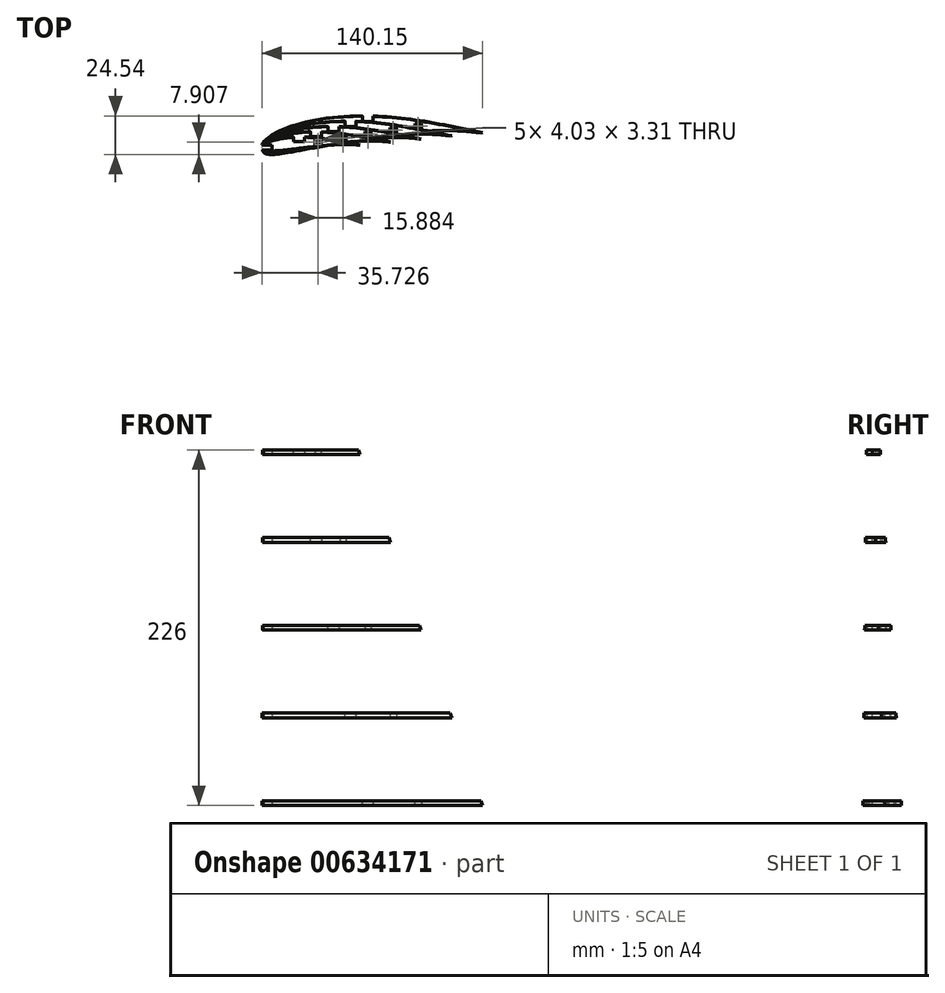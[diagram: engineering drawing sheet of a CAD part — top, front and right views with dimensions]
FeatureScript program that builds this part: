
annotation { "Feature Type Name" : "Feature", "Feature Type Description" : "" }
export const myFeature = defineFeature(function(context is Context, id is Id, definition is map)
    precondition{}
    {
        {
            var Q0;
            Q0=qCreatedBy(makeId("Top.planeOp"),FACE);
            var sketch = newSketch(context, id + "F0", { "sketchPlane" : qUnion([Q0])});
            skLineSegment(sketch, "E0", {"start": v(-0.42, 1.1) * mm, "end": v(1.04, 2.87) * mm});
            skLineSegment(sketch, "E1", {"start": v(1.04, 2.87) * mm, "end": v(2.54, 4.58) * mm});
            skLineSegment(sketch, "E2", {"start": v(2.54, 4.58) * mm, "end": v(4.15, 6.16) * mm});
            skLineSegment(sketch, "E3", {"start": v(4.15, 6.16) * mm, "end": v(4.64, 6.58) * mm});
            skLineSegment(sketch, "E4", {"start": v(4.64, 6.58) * mm, "end": v(5.9, 7.56) * mm});
            skLineSegment(sketch, "E5", {"start": v(5.9, 7.56) * mm, "end": v(7.8, 8.78) * mm});
            skLineSegment(sketch, "E6", {"start": v(7.8, 8.78) * mm, "end": v(9.8, 9.86) * mm});
            skLineSegment(sketch, "E7", {"start": v(9.8, 9.86) * mm, "end": v(11.89, 10.8) * mm});
            skLineSegment(sketch, "E8", {"start": v(11.89, 10.8) * mm, "end": v(15.88, 12.34) * mm});
            skLineSegment(sketch, "E9", {"start": v(15.88, 12.34) * mm, "end": v(18.36, 13.2) * mm});
            skLineSegment(sketch, "E10", {"start": v(18.36, 13.2) * mm, "end": v(22.7, 14.6) * mm});
            skLineSegment(sketch, "E11", {"start": v(22.7, 14.6) * mm, "end": v(27.05, 15.83) * mm});
            skLineSegment(sketch, "E12", {"start": v(27.05, 15.83) * mm, "end": v(32.46, 17.12) * mm});
            skLineSegment(sketch, "E13", {"start": v(32.46, 17.12) * mm, "end": v(35.87, 17.8) * mm});
            skLineSegment(sketch, "E14", {"start": v(35.87, 17.8) * mm, "end": v(40.34, 18.53) * mm});
            skLineSegment(sketch, "E15", {"start": v(40.34, 18.53) * mm, "end": v(44.84, 19.11) * mm});
            skLineSegment(sketch, "E16", {"start": v(44.84, 19.11) * mm, "end": v(49.37, 19.56) * mm});
            skLineSegment(sketch, "E17", {"start": v(49.37, 19.56) * mm, "end": v(52.55, 19.79) * mm});
            skLineSegment(sketch, "E18", {"start": v(52.55, 19.79) * mm, "end": v(58.48, 20.07) * mm});
            skLineSegment(sketch, "E19", {"start": v(58.48, 20.07) * mm, "end": v(63.03, 20.16) * mm});
            skLineSegment(sketch, "E20", {"start": v(63.03, 20.16) * mm, "end": v(67.58, 20.14) * mm});
            skLineSegment(sketch, "E21", {"start": v(67.58, 20.14) * mm, "end": v(72.1, 20.03) * mm});
            skLineSegment(sketch, "E22", {"start": v(72.1, 20.03) * mm, "end": v(74.6, 19.93) * mm});
            skLineSegment(sketch, "E23", {"start": v(74.6, 19.93) * mm, "end": v(81.02, 19.54) * mm});
            skLineSegment(sketch, "E24", {"start": v(81.02, 19.54) * mm, "end": v(85.48, 19.16) * mm});
            skLineSegment(sketch, "E25", {"start": v(85.48, 19.16) * mm, "end": v(90, 18.69) * mm});
            skLineSegment(sketch, "E26", {"start": v(90, 18.69) * mm, "end": v(96.67, 17.82) * mm});
            skLineSegment(sketch, "E27", {"start": v(96.67, 17.82) * mm, "end": v(99.3, 17.44) * mm});
            skLineSegment(sketch, "E28", {"start": v(99.3, 17.44) * mm, "end": v(104.05, 16.68) * mm});
            skLineSegment(sketch, "E29", {"start": v(104.05, 16.68) * mm, "end": v(108.68, 15.9) * mm});
            skLineSegment(sketch, "E30", {"start": v(108.68, 15.9) * mm, "end": v(110.9, 15.5) * mm});
            skLineSegment(sketch, "E31", {"start": v(110.9, 15.5) * mm, "end": v(113.04, 15.11) * mm});
            skLineSegment(sketch, "E32", {"start": v(113.04, 15.11) * mm, "end": v(115.07, 14.74) * mm});
            skLineSegment(sketch, "E33", {"start": v(115.07, 14.74) * mm, "end": v(116.62, 14.45) * mm});
            skLineSegment(sketch, "E34", {"start": v(116.62, 14.45) * mm, "end": v(120.51, 13.7) * mm});
            skLineSegment(sketch, "E35", {"start": v(120.51, 13.7) * mm, "end": v(122.38, 13.34) * mm});
            skLineSegment(sketch, "E36", {"start": v(122.38, 13.34) * mm, "end": v(123.38, 13.14) * mm});
            skLineSegment(sketch, "E37", {"start": v(123.38, 13.14) * mm, "end": v(124.45, 12.92) * mm});
            skLineSegment(sketch, "E38", {"start": v(124.45, 12.92) * mm, "end": v(125.6, 12.68) * mm});
            skLineSegment(sketch, "E39", {"start": v(125.6, 12.68) * mm, "end": v(126.84, 12.43) * mm});
            skLineSegment(sketch, "E40", {"start": v(126.84, 12.43) * mm, "end": v(128.18, 12.15) * mm});
            skLineSegment(sketch, "E41", {"start": v(128.18, 12.15) * mm, "end": v(129.65, 11.84) * mm});
            skLineSegment(sketch, "E42", {"start": v(129.65, 11.84) * mm, "end": v(131.93, 11.36) * mm});
            skLineSegment(sketch, "E43", {"start": v(131.93, 11.36) * mm, "end": v(133, 11.13) * mm});
            skLineSegment(sketch, "E44", {"start": v(133, 11.13) * mm, "end": v(134.82, 10.75) * mm});
            skLineSegment(sketch, "E45", {"start": v(134.82, 10.75) * mm, "end": v(136.58, 10.37) * mm});
            skLineSegment(sketch, "E46", {"start": v(136.58, 10.37) * mm, "end": v(137.4, 10.2) * mm});
            skLineSegment(sketch, "E47", {"start": v(137.4, 10.2) * mm, "end": v(138.16, 10.03) * mm});
            skLineSegment(sketch, "E48", {"start": v(138.16, 10.03) * mm, "end": v(138.83, 9.88) * mm});
            skLineSegment(sketch, "E49", {"start": v(138.83, 9.88) * mm, "end": v(139.4, 9.75) * mm});
            skLineSegment(sketch, "E50", {"start": v(139.4, 9.75) * mm, "end": v(139.86, 9.65) * mm});
            skLineSegment(sketch, "E51", {"start": v(139.86, 9.65) * mm, "end": v(140.2, 9.56) * mm});
            skLineSegment(sketch, "E52", {"start": v(140.2, 9.56) * mm, "end": v(140.38, 9.51) * mm});
            skLineSegment(sketch, "E53", {"start": v(140.38, 9.51) * mm, "end": v(140.4, 9.5) * mm});
            skLineSegment(sketch, "E54", {"start": v(140.4, 9.5) * mm, "end": v(140.24, 9.5) * mm});
            skLineSegment(sketch, "E55", {"start": v(140.24, 9.5) * mm, "end": v(140.08, 9.53) * mm});
            skLineSegment(sketch, "E56", {"start": v(140.08, 9.53) * mm, "end": v(139.36, 9.65) * mm});
            skLineSegment(sketch, "E57", {"start": v(139.36, 9.65) * mm, "end": v(138.4, 9.81) * mm});
            skLineSegment(sketch, "E58", {"start": v(138.4, 9.81) * mm, "end": v(136.21, 10.13) * mm});
            skLineSegment(sketch, "E59", {"start": v(136.21, 10.13) * mm, "end": v(133.85, 10.4) * mm});
            skLineSegment(sketch, "E60", {"start": v(133.85, 10.4) * mm, "end": v(131.61, 10.58) * mm});
            skLineSegment(sketch, "E61", {"start": v(131.61, 10.58) * mm, "end": v(126.03, 10.8) * mm});
            skLineSegment(sketch, "E62", {"start": v(126.03, 10.8) * mm, "end": v(122.98, 10.85) * mm});
            skLineSegment(sketch, "E63", {"start": v(122.98, 10.85) * mm, "end": v(118.52, 10.88) * mm});
            skLineSegment(sketch, "E64", {"start": v(118.52, 10.88) * mm, "end": v(113.95, 10.85) * mm});
            skLineSegment(sketch, "E65", {"start": v(113.95, 10.85) * mm, "end": v(109.34, 10.75) * mm});
            skLineSegment(sketch, "E66", {"start": v(109.34, 10.75) * mm, "end": v(103.97, 10.52) * mm});
            skLineSegment(sketch, "E67", {"start": v(103.97, 10.52) * mm, "end": v(100.13, 10.27) * mm});
            skLineSegment(sketch, "E68", {"start": v(100.13, 10.27) * mm, "end": v(95.58, 9.9) * mm});
            skLineSegment(sketch, "E69", {"start": v(95.58, 9.9) * mm, "end": v(91.07, 9.44) * mm});
            skLineSegment(sketch, "E70", {"start": v(91.07, 9.44) * mm, "end": v(86.57, 8.91) * mm});
            skLineSegment(sketch, "E71", {"start": v(86.57, 8.91) * mm, "end": v(76.85, 7.57) * mm});
            skLineSegment(sketch, "E72", {"start": v(76.85, 7.57) * mm, "end": v(68.73, 6.27) * mm});
            skLineSegment(sketch, "E73", {"start": v(68.73, 6.27) * mm, "end": v(59.8, 4.7) * mm});
            skLineSegment(sketch, "E74", {"start": v(59.8, 4.7) * mm, "end": v(49.88, 2.79) * mm});
            skLineSegment(sketch, "E75", {"start": v(49.88, 2.79) * mm, "end": v(41.82, 1.14) * mm});
            skLineSegment(sketch, "E76", {"start": v(41.82, 1.14) * mm, "end": v(37.34, 0.22) * mm});
            skLineSegment(sketch, "E77", {"start": v(37.34, 0.22) * mm, "end": v(32.9, -0.65) * mm});
            skLineSegment(sketch, "E78", {"start": v(32.9, -0.65) * mm, "end": v(26.98, -1.7) * mm});
            skLineSegment(sketch, "E79", {"start": v(26.98, -1.7) * mm, "end": v(24.24, -2.14) * mm});
            skLineSegment(sketch, "E80", {"start": v(24.24, -2.14) * mm, "end": v(19.94, -2.77) * mm});
            skLineSegment(sketch, "E81", {"start": v(19.94, -2.77) * mm, "end": v(17.73, -3.06) * mm});
            skLineSegment(sketch, "E82", {"start": v(17.73, -3.06) * mm, "end": v(15.45, -3.36) * mm});
            skLineSegment(sketch, "E83", {"start": v(15.45, -3.36) * mm, "end": v(13.08, -3.65) * mm});
            skLineSegment(sketch, "E84", {"start": v(13.08, -3.65) * mm, "end": v(10.68, -3.96) * mm});
            skLineSegment(sketch, "E85", {"start": v(10.68, -3.96) * mm, "end": v(8.03, -4.25) * mm});
            skLineSegment(sketch, "E86", {"start": v(8.03, -4.25) * mm, "end": v(6.75, -4.33) * mm});
            skLineSegment(sketch, "E87", {"start": v(6.75, -4.33) * mm, "end": v(5.52, -4.33) * mm});
            skLineSegment(sketch, "E88", {"start": v(5.52, -4.33) * mm, "end": v(4.36, -4.21) * mm});
            skLineSegment(sketch, "E89", {"start": v(4.36, -4.21) * mm, "end": v(3.3, -3.97) * mm});
            skLineSegment(sketch, "E90", {"start": v(3.3, -3.97) * mm, "end": v(2.34, -3.56) * mm});
            skLineSegment(sketch, "E91", {"start": v(2.34, -3.56) * mm, "end": v(1.92, -3.28) * mm});
            skLineSegment(sketch, "E92", {"start": v(1.92, -3.28) * mm, "end": v(1.4, -2.83) * mm});
            skLineSegment(sketch, "E93", {"start": v(1.4, -2.83) * mm, "end": v(1.19, -2.58) * mm});
            skLineSegment(sketch, "E94", {"start": v(1.19, -2.58) * mm, "end": v(0.89, -2.15) * mm});
            skLineSegment(sketch, "E95", {"start": v(0.89, -2.15) * mm, "end": v(0.38, -1.16) * mm});
            skLineSegment(sketch, "E96", {"start": v(0.38, -1.16) * mm, "end": v(-0.05, -0.06) * mm});
            skLineSegment(sketch, "E97", {"start": v(-0.05, -0.06) * mm, "end": v(-0.42, 1.1) * mm});
            skSolve(sketch);
        }
        {
            var Q0;
            Q0=qCreatedBy(makeId("Top.planeOp"),FACE);
            var sketch = newSketch(context, id + "F1", { "sketchPlane" : qUnion([Q0])});
            skPoint(sketch, "E98.0", {"position": v(0.94, -2.52) * mm});
            skPoint(sketch, "E98.1", {"position": v(0.64, -2.08) * mm});
            skPoint(sketch, "E98.2", {"position": v(0.13, -1.1) * mm});
            skPoint(sketch, "E98.3", {"position": v(0.8, 2.93) * mm});
            skPoint(sketch, "E98.5", {"position": v(40.1, 18.6) * mm});
            skPoint(sketch, "E98.6", {"position": v(85.24, 19.22) * mm});
            skPoint(sketch, "E98.7", {"position": v(140.15, 9.56) * mm});
            skPoint(sketch, "E98.8", {"position": v(125.78, 10.86) * mm});
            skPoint(sketch, "E98.9", {"position": v(99.89, 10.34) * mm});
            skPoint(sketch, "E98.10", {"position": v(49.63, 2.85) * mm});
            skPoint(sketch, "E98.11", {"position": v(12.84, -3.6) * mm});
            skPoint(sketch, "E98.12", {"position": v(2.1, -3.5) * mm});
            skPoint(sketch, "E98.13", {"position": v(5.28, -4.26) * mm});
            skFitSpline(sketch, "E99", {"points": [v(0.94, -2.52) * mm, v(2.1, -3.5) * mm, v(5.28, -4.26) * mm, v(12.84, -3.6) * mm, v(49.63, 2.85) * mm, v(99.89, 10.34) * mm, v(125.78, 10.86) * mm, v(140.15, 9.56) * mm], "startDerivative": vector(21.8, -23.84) * mm, "endDerivative": vector(100.11, -11.16) * mm});
            skPoint(sketch, "E100.0", {"position": v(11.64, 10.87) * mm});
            skFitSpline(sketch, "E101", {"points": [v(0.94, -2.52) * mm, v(0.64, -2.08) * mm, v(0.13, -1.1) * mm, v(0.8, 2.93) * mm, v(11.64, 10.87) * mm, v(40.1, 18.6) * mm, v(85.24, 19.22) * mm, v(140.15, 9.56) * mm], "startDerivative": vector(-10.5, 15.16) * mm, "endDerivative": vector(201.75, -43.18) * mm});
            skSolve(sketch);
        }
        {
            var Q0;
            Q0=qCreatedBy(makeId("Top.planeOp"),FACE);
            cPlane(context, id + "F2", {"entities" : qUnion([Q0]), "cplaneType" : CPlaneType.OFFSET, "offset" : 226 * mm, "width" : 150 * mm, "height" : 150 * mm});
        }
        {
            var Q0;
            Q0=qCreatedBy(id+"F2.planeOp",FACE);
            var sketch = newSketch(context, id + "F3", { "sketchPlane" : qUnion([Q0])});
            skPoint(sketch, "E102.0", {"position": v(0.64, -1.21) * mm});
            skPoint(sketch, "E102.1", {"position": v(0.07, -0.47) * mm});
            skPoint(sketch, "E102.2", {"position": v(0.27, 1.18) * mm});
            skPoint(sketch, "E102.3", {"position": v(2.53, 3.05) * mm});
            skPoint(sketch, "E102.4", {"position": v(15.91, 6.32) * mm});
            skPoint(sketch, "E102.5", {"position": v(32.82, 6.27) * mm});
            skPoint(sketch, "E102.6", {"position": v(61.27, 1.72) * mm});
            skPoint(sketch, "E102.7", {"position": v(55.5, 2.19) * mm});
            skPoint(sketch, "E102.8", {"position": v(33.37, 0.87) * mm});
            skPoint(sketch, "E102.9", {"position": v(18.25, -1.04) * mm});
            skPoint(sketch, "E102.10", {"position": v(10.5, -1.8) * mm});
            skPoint(sketch, "E102.11", {"position": v(1.43, -1.7) * mm});
            skPoint(sketch, "E102.12", {"position": v(2.88, -2) * mm});
            skFitSpline(sketch, "E103", {"points": [v(0.64, -1.21) * mm, v(0.07, -0.47) * mm, v(0.27, 1.18) * mm, v(2.53, 3.05) * mm, v(15.91, 6.32) * mm, v(32.82, 6.27) * mm, v(61.27, 1.72) * mm], "startDerivative": vector(-12.39, 11.02) * mm, "endDerivative": vector(97.43, -17.58) * mm});
            skFitSpline(sketch, "E104", {"points": [v(0.64, -1.21) * mm, v(1.43, -1.7) * mm, v(2.88, -2) * mm, v(10.5, -1.8) * mm, v(18.25, -1.04) * mm, v(33.37, 0.87) * mm, v(55.5, 2.19) * mm, v(61.27, 1.72) * mm], "startDerivative": vector(14.9, -10.52) * mm, "endDerivative": vector(36.47, -4.99) * mm});
            skSolve(sketch);
        }
        {
            var Q0;
            Q0=makeQuery(id+"F1.imprint","IMPRINT",FACE,{"disambiguationData":[TD([[makeQuery(id+"F1.imprint","IMPRINT",EDGE,{"derivedFrom":sQuery(id+"F1.wireOp",EDGE,"E99")}),1.0]])]});
            var Q1;
            Q1=makeQuery(id+"F3.imprint","IMPRINT",FACE,{"disambiguationData":[TD([[makeQuery(id+"F3.imprint","IMPRINT",EDGE,{"derivedFrom":sQuery(id+"F3.wireOp",EDGE,"E103")}),-1.0]])]});
            loft(context, id + "F4", {"sheetProfilesArray" : [{ "sheetProfileEntities" : qUnion([Q0]) }, { "sheetProfileEntities" : qUnion([Q1]) }]});
        }
        {
            var Q0;
            Q0=qCreatedBy(makeId("Front.planeOp"),FACE);
            var sketch = newSketch(context, id + "F5", { "sketchPlane" : qUnion([Q0])});
            skLineSegment(sketch, "E105", {"start": v(0, 0) * mm, "end": v(0, 3) * mm, "construction": true});
            skLineSegment(sketch, "E106.bottom", {"start": v(-6.3, 3) * mm, "end": v(175.34, 3) * mm});
            skLineSegment(sketch, "E106.top", {"start": v(-6.3, 55.75) * mm, "end": v(175.34, 55.75) * mm});
            skLineSegment(sketch, "E106.left", {"start": v(-6.3, 3) * mm, "end": v(-6.3, 55.75) * mm});
            skLineSegment(sketch, "E106.right", {"start": v(175.34, 3) * mm, "end": v(175.34, 55.75) * mm});
            skLineSegment(sketch, "E107.0.1.0", {"start": v(175.34, 58.75) * mm, "end": v(175.34, 111.5) * mm});
            skLineSegment(sketch, "E107.0.1.1", {"start": v(-6.3, 58.75) * mm, "end": v(-6.3, 111.5) * mm});
            skLineSegment(sketch, "E107.0.1.2", {"start": v(-6.3, 58.75) * mm, "end": v(175.34, 58.75) * mm});
            skLineSegment(sketch, "E107.0.1.3", {"start": v(-6.3, 111.5) * mm, "end": v(175.34, 111.5) * mm});
            skLineSegment(sketch, "E107.0.1.4", {"start": v(0, 55.75) * mm, "end": v(0, 58.75) * mm, "construction": true});
            skLineSegment(sketch, "E107.0.2.0", {"start": v(175.34, 114.5) * mm, "end": v(175.34, 167.25) * mm});
            skLineSegment(sketch, "E107.0.2.1", {"start": v(-6.3, 114.5) * mm, "end": v(-6.3, 167.25) * mm});
            skLineSegment(sketch, "E107.0.2.2", {"start": v(-6.3, 114.5) * mm, "end": v(175.34, 114.5) * mm});
            skLineSegment(sketch, "E107.0.2.3", {"start": v(-6.3, 167.25) * mm, "end": v(175.34, 167.25) * mm});
            skLineSegment(sketch, "E107.0.2.4", {"start": v(0, 111.5) * mm, "end": v(0, 114.5) * mm, "construction": true});
            skLineSegment(sketch, "E107.0.3.0", {"start": v(175.34, 170.25) * mm, "end": v(175.34, 223) * mm});
            skLineSegment(sketch, "E107.0.3.1", {"start": v(-6.3, 170.25) * mm, "end": v(-6.3, 223) * mm});
            skLineSegment(sketch, "E107.0.3.2", {"start": v(-6.3, 170.25) * mm, "end": v(175.34, 170.25) * mm});
            skLineSegment(sketch, "E107.0.3.3", {"start": v(-6.3, 223) * mm, "end": v(175.34, 223) * mm});
            skLineSegment(sketch, "E107.0.3.4", {"start": v(0, 167.25) * mm, "end": v(0, 170.25) * mm, "construction": true});
            skLineSegment(sketch, "E107.direction1", {"start": v(-6.3, 3) * mm, "end": v(18.7, 3) * mm, "construction": true});
            skLineSegment(sketch, "E107.direction2", {"start": v(-6.3, 3) * mm, "end": v(-6.3, 58.75) * mm, "construction": true});
            skSolve(sketch);
        }
        {
            var Q0;
            Q0 = qSketchRegion(id + "F5", true);
            extrude(context, id + "F6", {"entities" : qUnion([Q0]), "operationType" : NewBodyOperationType.REMOVE, "oppositeDirection" : true, "depth" : 50 * mm, "offsetDistance" : 25 * mm, "hasSecondDirection" : true, "secondDirectionOppositeDirection" : false, "secondDirectionDepth" : 50 * mm});
        }
        {
            var Q0;
            Q0=qCreatedBy(makeId("Top.planeOp"),FACE);
            var sketch = newSketch(context, id + "F7", { "sketchPlane" : qUnion([Q0])});
            skLineSegment(sketch, "E108", {"start": v(0, 0) * mm, "end": v(6.35, 0) * mm, "construction": true});
            skLineSegment(sketch, "E109", {"start": v(6.35, 0) * mm, "end": v(6.35, 1.59) * mm});
            skLineSegment(sketch, "E110", {"start": v(6.35, 0) * mm, "end": v(6.35, -1.59) * mm});
            skLineSegment(sketch, "E111", {"start": v(6.35, -1.59) * mm, "end": v(0, -1.59) * mm});
            skLineSegment(sketch, "E112", {"start": v(0, -1.59) * mm, "end": v(0, 1.59) * mm});
            skLineSegment(sketch, "E113", {"start": v(0, 1.59) * mm, "end": v(6.35, 1.59) * mm});
            skSolve(sketch);
        }
        {
            var Q0;
            Q0 = qSketchRegion(id + "F7", true);
            extrude(context, id + "F8", {"entities" : qUnion([Q0]), "operationType" : NewBodyOperationType.REMOVE, "depth" : 226 * mm, "offsetDistance" : 25 * mm});
        }
        {
            var Q0;
            Q0=makeQuery(id+"F4.opLoft","CAP_FACE",FACE,{"disambiguationData":[OSD([makeQuery(id+"F1.imprint","IMPRINT",FACE,{"disambiguationData":[TD([[makeQuery(id+"F1.imprint","IMPRINT",EDGE,{"derivedFrom":sQuery(id+"F1.wireOp",EDGE,"E99")}),1.0]])]})])],"isStart":true});
            var sketch = newSketch(context, id + "F9", { "sketchPlane" : qUnion([Q0])});
            skPoint(sketch, "E114.0", {"position": v(67.58, -20.14) * mm});
            skLineSegment(sketch, "E115", {"start": v(67.58, -20.14) * mm, "end": v(67.58, -16.97) * mm, "construction": true});
            skLineSegment(sketch, "E116", {"start": v(67.58, -16.97) * mm, "end": v(64.4, -16.97) * mm});
            skLineSegment(sketch, "E117", {"start": v(67.58, -16.97) * mm, "end": v(70.75, -16.97) * mm});
            skLineSegment(sketch, "E118", {"start": v(70.75, -16.97) * mm, "end": v(70.75, -20.47) * mm});
            skLineSegment(sketch, "E119", {"start": v(70.75, -20.47) * mm, "end": v(64.4, -20.47) * mm});
            skLineSegment(sketch, "E120", {"start": v(64.4, -20.47) * mm, "end": v(64.4, -16.97) * mm});
            skSolve(sketch);
        }
        {
            var Q0;
            Q0=makeQuery(id+"F3.imprint","IMPRINT",FACE,{"disambiguationData":[TD([[makeQuery(id+"F3.imprint","IMPRINT",EDGE,{"derivedFrom":sQuery(id+"F3.wireOp",EDGE,"E103")}),-1.0]])]});
            var sketch = newSketch(context, id + "F10", { "sketchPlane" : qUnion([Q0])});
            skFitSpline(sketch, "E121.0", {"points": [v(62.32, 1.83) * mm, v(59.72, 2.3) * mm, v(54.52, 3.24) * mm, v(46.72, 4.6) * mm, v(40.2, 5.61) * mm, v(34.96, 6.3) * mm, v(31.03, 6.7) * mm, v(27.08, 6.97) * mm, v(23.1, 7.03) * mm, v(19.18, 6.84) * mm, v(15.94, 6.47) * mm, v(13.37, 6.05) * mm, v(11.45, 5.7) * mm, v(9.54, 5.29) * mm, v(7.63, 4.82) * mm, v(5.74, 4.3) * mm, v(4.17, 3.78) * mm, v(2.93, 3.29) * mm, v(2.18, 2.93) * mm, v(1.6, 2.6) * mm, v(1.19, 2.31) * mm, v(0.81, 1.98) * mm, v(0.6, 1.73) * mm, v(0.5, 1.59) * mm]});
            skLineSegment(sketch, "E122", {"start": v(23.23, 7) * mm, "end": v(23.23, 3.82) * mm, "construction": true});
            skLineSegment(sketch, "E123", {"start": v(23.23, 3.82) * mm, "end": v(26.4, 3.82) * mm});
            skLineSegment(sketch, "E124", {"start": v(23.23, 3.82) * mm, "end": v(20.06, 3.82) * mm});
            skLineSegment(sketch, "E125", {"start": v(26.4, 3.82) * mm, "end": v(26.4, 7.32) * mm});
            skLineSegment(sketch, "E126", {"start": v(26.4, 7.32) * mm, "end": v(20.06, 7.32) * mm});
            skLineSegment(sketch, "E127", {"start": v(20.06, 7.32) * mm, "end": v(20.06, 3.82) * mm});
            skSolve(sketch);
        }
        {
            var Q0;
            Q0=makeQuery(id+"F1.imprint","IMPRINT",FACE,{"disambiguationData":[TD([[makeQuery(id+"F1.imprint","IMPRINT",EDGE,{"derivedFrom":sQuery(id+"F1.wireOp",EDGE,"E99")}),1.0]])]});
            var sketch = newSketch(context, id + "F11", { "sketchPlane" : qUnion([Q0])});
            skPoint(sketch, "E128.0", {"position": v(70.75, 16.97) * mm});
            skPoint(sketch, "E128.1", {"position": v(64.4, 16.97) * mm});
            skPoint(sketch, "E128.2", {"position": v(64.4, 20.47) * mm});
            skPoint(sketch, "E128.3", {"position": v(70.75, 20.47) * mm});
            skLineSegment(sketch, "E129", {"start": v(70.75, 20.47) * mm, "end": v(70.75, 16.97) * mm});
            skLineSegment(sketch, "E130", {"start": v(70.75, 16.97) * mm, "end": v(64.4, 16.97) * mm});
            skLineSegment(sketch, "E131", {"start": v(64.4, 16.97) * mm, "end": v(64.4, 20.47) * mm});
            skLineSegment(sketch, "E132", {"start": v(64.4, 20.47) * mm, "end": v(70.75, 20.47) * mm});
            skSolve(sketch);
        }
        {
            var Q0;
            Q0=makeQuery(id+"F3.imprint","IMPRINT",FACE,{"disambiguationData":[TD([[makeQuery(id+"F3.imprint","IMPRINT",EDGE,{"derivedFrom":sQuery(id+"F3.wireOp",EDGE,"E103")}),-1.0]])]});
            var sketch = newSketch(context, id + "F12", { "sketchPlane" : qUnion([Q0])});
            skPoint(sketch, "E133.0", {"position": v(20.06, 7.32) * mm});
            skPoint(sketch, "E133.1", {"position": v(20.06, 3.82) * mm});
            skPoint(sketch, "E133.2", {"position": v(26.4, 3.82) * mm});
            skPoint(sketch, "E133.3", {"position": v(26.4, 7.32) * mm});
            skLineSegment(sketch, "E134.bottom", {"start": v(20.06, 3.82) * mm, "end": v(26.4, 3.82) * mm});
            skLineSegment(sketch, "E134.top", {"start": v(20.06, 7.32) * mm, "end": v(26.4, 7.32) * mm});
            skLineSegment(sketch, "E134.left", {"start": v(20.06, 3.82) * mm, "end": v(20.06, 7.32) * mm});
            skLineSegment(sketch, "E134.right", {"start": v(26.4, 3.82) * mm, "end": v(26.4, 7.32) * mm});
            skSolve(sketch);
        }
        {
            var Q0;
            Q0 = qSketchRegion(id + "F11", true);
            var Q1;
            Q1 = qSketchRegion(id + "F12", true);
            loft(context, id + "F13", {"operationType" : NewBodyOperationType.REMOVE, "sheetProfilesArray" : [{ "sheetProfileEntities" : qUnion([Q0]) }, { "sheetProfileEntities" : qUnion([Q1]) }]});
        }
        {
            var Q0;
            Q0=makeQuery(id+"F1.imprint","IMPRINT",FACE,{"disambiguationData":[TD([[makeQuery(id+"F1.imprint","IMPRINT",EDGE,{"derivedFrom":sQuery(id+"F1.wireOp",EDGE,"E99")}),1.0]])]});
            var sketch = newSketch(context, id + "F14", { "sketchPlane" : qUnion([Q0])});
            skLineSegment(sketch, "E135.bottom", {"start": v(101.28, 15.47) * mm, "end": v(98.1, 15.47) * mm});
            skLineSegment(sketch, "E135.top", {"start": v(101.28, 12.3) * mm, "end": v(98.1, 12.3) * mm});
            skLineSegment(sketch, "E135.left", {"start": v(101.28, 15.47) * mm, "end": v(101.28, 12.3) * mm});
            skLineSegment(sketch, "E135.right", {"start": v(98.1, 15.47) * mm, "end": v(98.1, 12.3) * mm});
            skSolve(sketch);
        }
        {
            var Q0;
            Q0=makeQuery(id+"F3.imprint","IMPRINT",FACE,{"disambiguationData":[TD([[makeQuery(id+"F3.imprint","IMPRINT",EDGE,{"derivedFrom":sQuery(id+"F3.wireOp",EDGE,"E103")}),-1.0]])]});
            var sketch = newSketch(context, id + "F15", { "sketchPlane" : qUnion([Q0])});
            skLineSegment(sketch, "E136.bottom", {"start": v(33.71, 5.13) * mm, "end": v(36.89, 5.13) * mm});
            skLineSegment(sketch, "E136.top", {"start": v(33.71, 1.95) * mm, "end": v(36.89, 1.95) * mm});
            skLineSegment(sketch, "E136.left", {"start": v(33.71, 5.13) * mm, "end": v(33.71, 1.95) * mm});
            skLineSegment(sketch, "E136.right", {"start": v(36.89, 5.13) * mm, "end": v(36.89, 1.95) * mm});
            skSolve(sketch);
        }
        {
            var Q0;
            Q0 = qSketchRegion(id + "F14", true);
            var Q1;
            Q1 = qSketchRegion(id + "F15", true);
            loft(context, id + "F16", {"operationType" : NewBodyOperationType.REMOVE, "sheetProfilesArray" : [{ "sheetProfileEntities" : qUnion([Q0]) }, { "sheetProfileEntities" : qUnion([Q1]) }]});
        }
        {
            var Q0;
            Q0=makeQuery(id+"F4.opLoft","CAP_FACE",FACE,{"disambiguationData":[OSD([makeQuery(id+"F3.imprint","IMPRINT",FACE,{"disambiguationData":[TD([[makeQuery(id+"F3.imprint","IMPRINT",EDGE,{"derivedFrom":sQuery(id+"F3.wireOp",EDGE,"E103")}),-1.0]])]})])],"isStart":true});
            var sketch = newSketch(context, id + "F17", { "sketchPlane" : qUnion([Q0])});
            skLineSegment(sketch, "E137.0", {"start": v(20.06, 6.72) * mm, "end": v(20.06, 3.82) * mm});
            skLineSegment(sketch, "E137.1", {"start": v(20.06, 3.82) * mm, "end": v(26.4, 3.82) * mm});
            skLineSegment(sketch, "E137.2", {"start": v(33.71, 5.13) * mm, "end": v(33.71, 1.95) * mm});
            skLineSegment(sketch, "E137.3", {"start": v(36.89, 1.95) * mm, "end": v(36.89, 5.13) * mm});
            skLineSegment(sketch, "E138", {"start": v(26.4, 3.82) * mm, "end": v(26.4, 7.57) * mm});
            skLineSegment(sketch, "E139", {"start": v(26.4, 7.57) * mm, "end": v(20.06, 7.57) * mm});
            skLineSegment(sketch, "E140", {"start": v(20.06, 7.57) * mm, "end": v(20.06, 6.72) * mm});
            skLineSegment(sketch, "E141", {"start": v(33.71, 5.13) * mm, "end": v(36.89, 5.13) * mm});
            skLineSegment(sketch, "E142", {"start": v(36.89, 1.95) * mm, "end": v(33.71, 1.95) * mm});
            skSolve(sketch);
        }
        {
            var Q0;
            Q0 = qSketchRegion(id + "F17", true);
            extrude(context, id + "F18", {"entities" : qUnion([Q0]), "operationType" : NewBodyOperationType.REMOVE, "oppositeDirection" : true, "depth" : 25 * mm, "offsetDistance" : 25 * mm});
        }
        {
            var Q0;
            Q0=makeQuery(id+"F6.boolean.opBoolean","COPY",FACE,{"derivedFrom":makeQuery(id+"F6.opExtrude","SWEPT_FACE",FACE,{"disambiguationData":[OSD([sQuery(id+"F5.wireOp",EDGE,"E107.0.3.2")])]})});
            var sketch = newSketch(context, id + "F19", { "sketchPlane" : qUnion([Q0])});
            skLineSegment(sketch, "E143.0", {"start": v(31, 7.06) * mm, "end": v(31, 10.06) * mm});
            skLineSegment(sketch, "E143.1", {"start": v(37.35, 7.06) * mm, "end": v(31, 7.06) * mm});
            skLineSegment(sketch, "E143.2", {"start": v(49.6, 4.5) * mm, "end": v(49.6, 7.68) * mm});
            skLineSegment(sketch, "E143.3", {"start": v(52.77, 7.68) * mm, "end": v(52.77, 4.5) * mm});
            skLineSegment(sketch, "E144", {"start": v(37.35, 7.06) * mm, "end": v(37.35, 11.42) * mm});
            skLineSegment(sketch, "E145", {"start": v(37.35, 11.42) * mm, "end": v(31, 11.42) * mm});
            skLineSegment(sketch, "E146", {"start": v(31, 11.42) * mm, "end": v(31, 10.06) * mm});
            skLineSegment(sketch, "E147", {"start": v(49.6, 7.68) * mm, "end": v(52.77, 7.68) * mm});
            skLineSegment(sketch, "E148", {"start": v(52.77, 4.5) * mm, "end": v(49.6, 4.5) * mm});
            skSolve(sketch);
        }
        {
            var Q0;
            Q0 = qSketchRegion(id + "F19", true);
            extrude(context, id + "F20", {"entities" : qUnion([Q0]), "operationType" : NewBodyOperationType.REMOVE, "oppositeDirection" : true, "depth" : 25 * mm, "offsetDistance" : 25 * mm});
        }
        {
            var Q0;
            Q0=makeQuery(id+"F6.boolean.opBoolean","COPY",FACE,{"derivedFrom":makeQuery(id+"F6.opExtrude","SWEPT_FACE",FACE,{"disambiguationData":[OSD([sQuery(id+"F5.wireOp",EDGE,"E107.0.2.2")])]})});
            var sketch = newSketch(context, id + "F21", { "sketchPlane" : qUnion([Q0])});
            skLineSegment(sketch, "E149.0", {"start": v(41.93, 10.3) * mm, "end": v(41.93, 13.4) * mm});
            skLineSegment(sketch, "E149.1", {"start": v(48.28, 10.3) * mm, "end": v(41.93, 10.3) * mm});
            skLineSegment(sketch, "E149.2", {"start": v(65.48, 7.05) * mm, "end": v(65.48, 10.23) * mm});
            skLineSegment(sketch, "E149.3", {"start": v(68.65, 10.23) * mm, "end": v(68.65, 7.05) * mm});
            skLineSegment(sketch, "E150", {"start": v(48.28, 10.3) * mm, "end": v(48.28, 15.15) * mm});
            skLineSegment(sketch, "E151", {"start": v(48.28, 15.15) * mm, "end": v(41.93, 15.15) * mm});
            skLineSegment(sketch, "E152", {"start": v(41.93, 15.15) * mm, "end": v(41.93, 13.4) * mm});
            skLineSegment(sketch, "E153", {"start": v(65.48, 10.23) * mm, "end": v(68.65, 10.23) * mm});
            skLineSegment(sketch, "E154", {"start": v(68.65, 7.05) * mm, "end": v(65.48, 7.05) * mm});
            skSolve(sketch);
        }
        {
            var Q0;
            Q0 = qSketchRegion(id + "F21", true);
            extrude(context, id + "F22", {"entities" : qUnion([Q0]), "operationType" : NewBodyOperationType.REMOVE, "oppositeDirection" : true, "depth" : 25 * mm, "offsetDistance" : 25 * mm});
        }
        {
            var Q0;
            Q0=makeQuery(id+"F6.boolean.opBoolean","COPY",FACE,{"derivedFrom":makeQuery(id+"F6.opExtrude","SWEPT_FACE",FACE,{"disambiguationData":[OSD([sQuery(id+"F5.wireOp",EDGE,"E107.0.1.2")])]})});
            var sketch = newSketch(context, id + "F23", { "sketchPlane" : qUnion([Q0])});
            skLineSegment(sketch, "E155.0", {"start": v(52.87, 13.55) * mm, "end": v(52.87, 16.72) * mm});
            skLineSegment(sketch, "E155.1", {"start": v(59.22, 13.55) * mm, "end": v(52.87, 13.55) * mm});
            skLineSegment(sketch, "E155.2", {"start": v(81.36, 9.6) * mm, "end": v(81.36, 12.78) * mm});
            skLineSegment(sketch, "E155.3", {"start": v(84.54, 12.78) * mm, "end": v(84.54, 9.6) * mm});
            skLineSegment(sketch, "E156", {"start": v(59.22, 13.55) * mm, "end": v(59.22, 18.7) * mm});
            skLineSegment(sketch, "E157", {"start": v(59.22, 18.7) * mm, "end": v(52.87, 18.7) * mm});
            skLineSegment(sketch, "E158", {"start": v(52.87, 18.7) * mm, "end": v(52.87, 16.72) * mm});
            skLineSegment(sketch, "E159", {"start": v(81.36, 12.78) * mm, "end": v(84.54, 12.78) * mm});
            skLineSegment(sketch, "E160", {"start": v(81.36, 9.6) * mm, "end": v(84.54, 9.6) * mm});
            skSolve(sketch);
        }
        {
            var Q0;
            Q0 = qSketchRegion(id + "F23", true);
            extrude(context, id + "F24", {"entities" : qUnion([Q0]), "operationType" : NewBodyOperationType.REMOVE, "oppositeDirection" : true, "depth" : 25 * mm, "offsetDistance" : 25 * mm});
        }
        {
            var Q0;
            Q0=makeQuery(id+"F6.boolean.opBoolean","COPY",FACE,{"derivedFrom":makeQuery(id+"F6.opExtrude","SWEPT_FACE",FACE,{"disambiguationData":[OSD([sQuery(id+"F5.wireOp",EDGE,"E106.bottom")])]})});
            var sketch = newSketch(context, id + "F25", { "sketchPlane" : qUnion([Q0])});
            skLineSegment(sketch, "E161.0", {"start": v(63.81, 16.8) * mm, "end": v(63.81, 20.06) * mm});
            skLineSegment(sketch, "E161.1", {"start": v(70.16, 16.8) * mm, "end": v(63.81, 16.8) * mm});
            skLineSegment(sketch, "E161.2", {"start": v(97.25, 12.16) * mm, "end": v(97.25, 15.33) * mm});
            skLineSegment(sketch, "E161.3", {"start": v(100.42, 15.33) * mm, "end": v(100.42, 12.16) * mm});
            skLineSegment(sketch, "E162", {"start": v(70.16, 16.8) * mm, "end": v(70.16, 21.68) * mm});
            skLineSegment(sketch, "E163", {"start": v(70.16, 21.68) * mm, "end": v(63.81, 21.68) * mm});
            skLineSegment(sketch, "E164", {"start": v(63.81, 21.68) * mm, "end": v(63.81, 20.06) * mm});
            skLineSegment(sketch, "E165", {"start": v(97.25, 15.33) * mm, "end": v(100.42, 15.33) * mm});
            skLineSegment(sketch, "E166", {"start": v(100.42, 12.16) * mm, "end": v(97.25, 12.16) * mm});
            skSolve(sketch);
        }
        {
            var Q0;
            Q0 = qSketchRegion(id + "F25", true);
            extrude(context, id + "F26", {"entities" : qUnion([Q0]), "operationType" : NewBodyOperationType.REMOVE, "oppositeDirection" : true, "depth" : 25 * mm, "offsetDistance" : 25 * mm});
        }
        {
            var Q0;
            Q0=makeQuery(id+"F4.opLoft","CAP_FACE",FACE,{"disambiguationData":[OSD([makeQuery(id+"F1.imprint","IMPRINT",FACE,{"disambiguationData":[TD([[makeQuery(id+"F1.imprint","IMPRINT",EDGE,{"derivedFrom":sQuery(id+"F1.wireOp",EDGE,"E99")}),1.0]])]})])],"isStart":true});
            var sketch = newSketch(context, id + "F27", { "sketchPlane" : qUnion([Q0])});
            skLineSegment(sketch, "E167.0", {"start": v(70.75, -16.97) * mm, "end": v(70.75, -20.15) * mm});
            skLineSegment(sketch, "E167.1", {"start": v(70.16, -16.8) * mm, "end": v(63.81, -16.8) * mm});
            skLineSegment(sketch, "E168", {"start": v(70.16, -16.8) * mm, "end": v(70.75, -16.8) * mm});
            skLineSegment(sketch, "E169", {"start": v(70.75, -16.8) * mm, "end": v(70.75, -16.97) * mm});
            skLineSegment(sketch, "E170", {"start": v(63.81, -16.8) * mm, "end": v(63.81, -21.12) * mm});
            skLineSegment(sketch, "E171", {"start": v(63.81, -21.12) * mm, "end": v(70.75, -21.12) * mm});
            skLineSegment(sketch, "E172", {"start": v(70.75, -21.12) * mm, "end": v(70.75, -20.15) * mm});
            skLineSegment(sketch, "E173.0", {"start": v(97.25, -12.16) * mm, "end": v(97.25, -15.33) * mm});
            skLineSegment(sketch, "E173.1", {"start": v(101.28, -15.47) * mm, "end": v(98.1, -15.47) * mm});
            skLineSegment(sketch, "E174", {"start": v(97.25, -15.33) * mm, "end": v(97.25, -15.47) * mm});
            skLineSegment(sketch, "E175", {"start": v(97.25, -15.47) * mm, "end": v(98.1, -15.47) * mm});
            skLineSegment(sketch, "E176", {"start": v(101.28, -15.47) * mm, "end": v(101.28, -12.16) * mm});
            skPoint(sketch, "E176.endSnap0", {"position": v(98.83, -12.16) * mm});
            skLineSegment(sketch, "E177", {"start": v(101.28, -12.16) * mm, "end": v(97.25, -12.16) * mm});
            skSolve(sketch);
        }
        {
            var Q0;
            Q0 = qSketchRegion(id + "F27", true);
            extrude(context, id + "F28", {"entities" : qUnion([Q0]), "operationType" : NewBodyOperationType.REMOVE, "oppositeDirection" : true, "depth" : 25 * mm, "offsetDistance" : 25 * mm});
        }
        {
            var Q0;
            Q0=makeQuery(id+"F6.boolean.opBoolean","COPY",FACE,{"derivedFrom":makeQuery(id+"F6.opExtrude","SWEPT_FACE",FACE,{"disambiguationData":[OSD([sQuery(id+"F5.wireOp",EDGE,"E106.top")])]})});
            var sketch = newSketch(context, id + "F29", { "sketchPlane" : qUnion([Q0])});
            skLineSegment(sketch, "E178.0", {"start": v(52.87, -13.55) * mm, "end": v(59.22, -13.55) * mm});
            skLineSegment(sketch, "E178.1", {"start": v(59.81, -16.82) * mm, "end": v(59.81, -13.72) * mm});
            skLineSegment(sketch, "E178.2", {"start": v(81.36, -12.78) * mm, "end": v(81.36, -9.6) * mm});
            skLineSegment(sketch, "E178.3", {"start": v(82.22, -12.92) * mm, "end": v(85.4, -12.92) * mm});
            skLineSegment(sketch, "E179", {"start": v(59.22, -13.55) * mm, "end": v(59.81, -13.55) * mm});
            skLineSegment(sketch, "E180", {"start": v(59.81, -13.55) * mm, "end": v(59.81, -13.72) * mm});
            skLineSegment(sketch, "E181", {"start": v(59.81, -16.82) * mm, "end": v(59.81, -17.44) * mm});
            skLineSegment(sketch, "E182", {"start": v(59.81, -17.44) * mm, "end": v(52.87, -17.44) * mm});
            skLineSegment(sketch, "E183", {"start": v(52.87, -17.44) * mm, "end": v(52.87, -13.55) * mm});
            skLineSegment(sketch, "E184", {"start": v(81.36, -12.78) * mm, "end": v(81.36, -12.92) * mm});
            skLineSegment(sketch, "E185", {"start": v(81.36, -12.92) * mm, "end": v(82.22, -12.92) * mm});
            skLineSegment(sketch, "E186", {"start": v(85.4, -12.92) * mm, "end": v(85.4, -9.6) * mm});
            skLineSegment(sketch, "E187", {"start": v(85.4, -9.6) * mm, "end": v(81.36, -9.6) * mm});
            skSolve(sketch);
        }
        {
            var Q0;
            Q0 = qSketchRegion(id + "F29", true);
            extrude(context, id + "F30", {"entities" : qUnion([Q0]), "operationType" : NewBodyOperationType.REMOVE, "oppositeDirection" : true, "depth" : 25 * mm, "offsetDistance" : 25 * mm});
        }
        {
            var Q0;
            Q0=makeQuery(id+"F6.boolean.opBoolean","COPY",FACE,{"derivedFrom":makeQuery(id+"F6.opExtrude","SWEPT_FACE",FACE,{"disambiguationData":[OSD([sQuery(id+"F5.wireOp",EDGE,"E107.0.1.3")])]})});
            var sketch = newSketch(context, id + "F31", { "sketchPlane" : qUnion([Q0])});
            skLineSegment(sketch, "E188.0", {"start": v(41.93, -10.3) * mm, "end": v(48.28, -10.3) * mm});
            skLineSegment(sketch, "E188.1", {"start": v(48.87, -13.5) * mm, "end": v(48.87, -10.48) * mm});
            skLineSegment(sketch, "E188.2", {"start": v(65.48, -10.23) * mm, "end": v(65.48, -7.05) * mm});
            skLineSegment(sketch, "E188.3", {"start": v(66.33, -10.37) * mm, "end": v(69.5, -10.37) * mm});
            skLineSegment(sketch, "E189", {"start": v(48.87, -10.48) * mm, "end": v(48.87, -10.3) * mm});
            skLineSegment(sketch, "E190", {"start": v(48.87, -10.3) * mm, "end": v(48.28, -10.3) * mm});
            skLineSegment(sketch, "E191", {"start": v(41.93, -10.3) * mm, "end": v(41.93, -14.16) * mm});
            skLineSegment(sketch, "E192", {"start": v(41.93, -14.16) * mm, "end": v(48.87, -14.16) * mm});
            skLineSegment(sketch, "E193", {"start": v(48.87, -14.16) * mm, "end": v(48.87, -13.5) * mm});
            skLineSegment(sketch, "E194", {"start": v(65.48, -10.23) * mm, "end": v(65.48, -10.37) * mm});
            skLineSegment(sketch, "E195", {"start": v(65.48, -10.37) * mm, "end": v(66.33, -10.37) * mm});
            skLineSegment(sketch, "E196", {"start": v(69.5, -10.37) * mm, "end": v(69.5, -7.05) * mm});
            skPoint(sketch, "E196.endSnap0", {"position": v(67.07, -7.05) * mm});
            skLineSegment(sketch, "E197", {"start": v(69.5, -7.05) * mm, "end": v(65.48, -7.05) * mm});
            skSolve(sketch);
        }
        {
            var Q0;
            Q0 = qSketchRegion(id + "F31", true);
            extrude(context, id + "F32", {"entities" : qUnion([Q0]), "operationType" : NewBodyOperationType.REMOVE, "oppositeDirection" : true, "depth" : 25 * mm, "offsetDistance" : 25 * mm});
        }
        {
            var Q0;
            Q0=makeQuery(id+"F6.boolean.opBoolean","COPY",FACE,{"derivedFrom":makeQuery(id+"F6.opExtrude","SWEPT_FACE",FACE,{"disambiguationData":[OSD([sQuery(id+"F5.wireOp",EDGE,"E107.0.2.3")])]})});
            var sketch = newSketch(context, id + "F33", { "sketchPlane" : qUnion([Q0])});
            skLineSegment(sketch, "E198.0", {"start": v(31, -7.06) * mm, "end": v(37.35, -7.06) * mm});
            skLineSegment(sketch, "E198.1", {"start": v(37.93, -10.2) * mm, "end": v(37.93, -7.24) * mm});
            skLineSegment(sketch, "E198.2", {"start": v(49.6, -7.68) * mm, "end": v(49.6, -4.5) * mm});
            skLineSegment(sketch, "E198.3", {"start": v(50.45, -7.81) * mm, "end": v(53.62, -7.81) * mm});
            skLineSegment(sketch, "E199", {"start": v(37.35, -7.06) * mm, "end": v(37.93, -7.06) * mm});
            skLineSegment(sketch, "E200", {"start": v(37.93, -7.06) * mm, "end": v(37.93, -7.24) * mm});
            skLineSegment(sketch, "E201", {"start": v(31, -7.06) * mm, "end": v(31, -11.38) * mm});
            skLineSegment(sketch, "E202", {"start": v(31, -11.38) * mm, "end": v(37.93, -11.38) * mm});
            skLineSegment(sketch, "E203", {"start": v(37.93, -11.38) * mm, "end": v(37.93, -10.2) * mm});
            skLineSegment(sketch, "E204", {"start": v(49.6, -7.68) * mm, "end": v(49.6, -7.81) * mm});
            skLineSegment(sketch, "E205", {"start": v(49.6, -7.81) * mm, "end": v(50.45, -7.81) * mm});
            skLineSegment(sketch, "E206", {"start": v(53.62, -7.81) * mm, "end": v(53.62, -4.5) * mm});
            skLineSegment(sketch, "E207", {"start": v(53.62, -4.5) * mm, "end": v(49.6, -4.5) * mm});
            skSolve(sketch);
        }
        {
            var Q0;
            Q0 = qSketchRegion(id + "F33", true);
            extrude(context, id + "F34", {"entities" : qUnion([Q0]), "operationType" : NewBodyOperationType.REMOVE, "oppositeDirection" : true, "depth" : 25 * mm, "offsetDistance" : 25 * mm});
        }
        {
            var Q0;
            Q0=makeQuery(id+"F6.boolean.opBoolean","COPY",FACE,{"derivedFrom":makeQuery(id+"F6.opExtrude","SWEPT_FACE",FACE,{"disambiguationData":[OSD([sQuery(id+"F5.wireOp",EDGE,"E107.0.3.3")])]})});
            var sketch = newSketch(context, id + "F35", { "sketchPlane" : qUnion([Q0])});
            skLineSegment(sketch, "E208.0", {"start": v(26.4, -3.82) * mm, "end": v(20.06, -3.82) * mm});
            skLineSegment(sketch, "E208.1", {"start": v(27, -6.94) * mm, "end": v(27, -4) * mm});
            skLineSegment(sketch, "E208.2", {"start": v(33.71, -1.95) * mm, "end": v(33.71, -5.13) * mm});
            skLineSegment(sketch, "E208.3", {"start": v(34.57, -5.26) * mm, "end": v(37.74, -5.26) * mm});
            skLineSegment(sketch, "E209", {"start": v(26.4, -3.82) * mm, "end": v(27, -3.82) * mm});
            skLineSegment(sketch, "E210", {"start": v(27, -3.82) * mm, "end": v(27, -4) * mm});
            skLineSegment(sketch, "E211", {"start": v(20.06, -3.82) * mm, "end": v(20.06, -7.33) * mm});
            skLineSegment(sketch, "E212", {"start": v(20.06, -7.33) * mm, "end": v(27, -7.33) * mm});
            skLineSegment(sketch, "E213", {"start": v(27, -7.33) * mm, "end": v(27, -6.94) * mm});
            skLineSegment(sketch, "E214", {"start": v(33.71, -5.13) * mm, "end": v(33.71, -5.26) * mm});
            skLineSegment(sketch, "E215", {"start": v(33.71, -5.26) * mm, "end": v(34.57, -5.26) * mm});
            skLineSegment(sketch, "E216", {"start": v(37.74, -5.26) * mm, "end": v(37.74, -1.95) * mm});
            skPoint(sketch, "E216.endSnap0", {"position": v(35.3, -1.95) * mm});
            skLineSegment(sketch, "E217", {"start": v(37.74, -1.95) * mm, "end": v(33.71, -1.95) * mm});
            skSolve(sketch);
        }
        {
            var Q0;
            Q0 = qSketchRegion(id + "F35", true);
            extrude(context, id + "F36", {"entities" : qUnion([Q0]), "operationType" : NewBodyOperationType.REMOVE, "oppositeDirection" : true, "depth" : 25 * mm, "offsetDistance" : 25 * mm});
        }
    });
